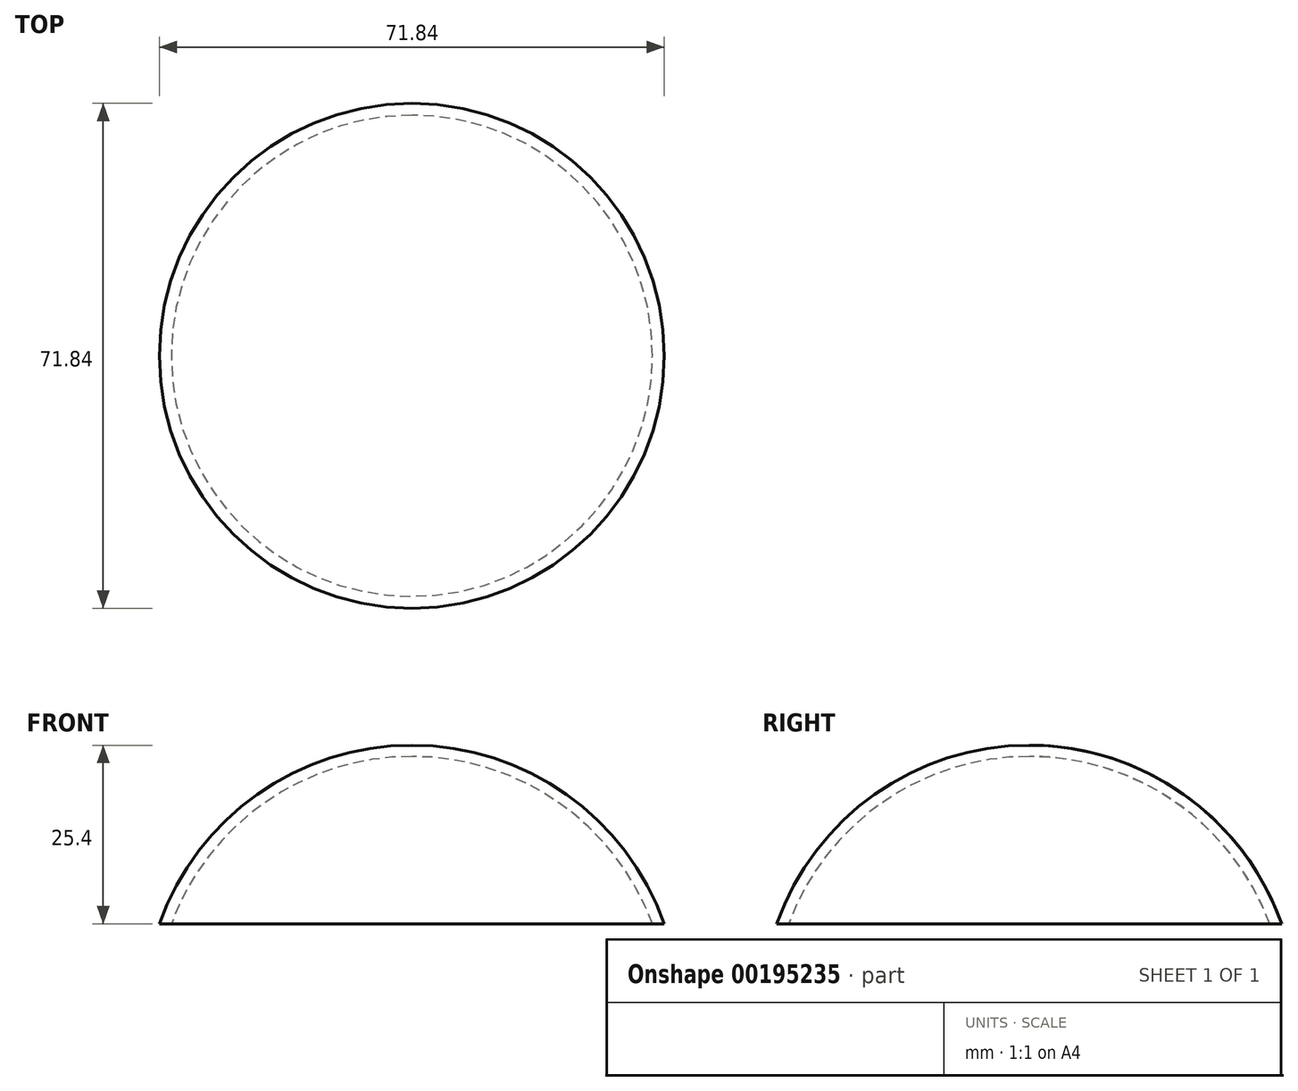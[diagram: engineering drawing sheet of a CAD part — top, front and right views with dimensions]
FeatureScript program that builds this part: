
annotation { "Feature Type Name" : "Feature", "Feature Type Description" : "" }
export const myFeature = defineFeature(function(context is Context, id is Id, definition is map)
    precondition{}
    {
        {
            var Q0;
            Q0=qCreatedBy(makeId("Right.planeOp"),FACE);
            var sketch = newSketch(context, id + "F0", { "sketchPlane" : qUnion([Q0])});
            skArc(sketch, "E0", {"start": v(38.1, 0) * mm, "mid": v(26.94, 26.94) * mm, "end": v(0, 38.1) * mm, "construction": true});
            skLineSegment(sketch, "E1", {"start": v(0, 38.1) * mm, "end": v(0, 0) * mm, "construction": true});
            skLineSegment(sketch, "E2", {"start": v(0, 0) * mm, "end": v(38.1, 0) * mm, "construction": true});
            skArc(sketch, "E3", {"start": v(36.51, 0) * mm, "mid": v(25.82, 25.82) * mm, "end": v(0, 36.51) * mm, "construction": true});
            skLineSegment(sketch, "E4", {"start": v(38.1, 0) * mm, "end": v(36.51, 0) * mm});
            skLineSegment(sketch, "E5", {"start": v(0, 36.51) * mm, "end": v(0, 38.1) * mm});
            skArc(sketch, "E6", {"start": v(34.23, 12.7) * mm, "mid": v(20.85, 29.97) * mm, "end": v(0, 36.51) * mm});
            skArc(sketch, "E7", {"start": v(35.92, 12.7) * mm, "mid": v(22, 31.1) * mm, "end": v(0, 38.1) * mm});
            skLineSegment(sketch, "E8", {"start": v(35.92, 12.7) * mm, "end": v(34.23, 12.7) * mm});
            skSolve(sketch);
        }
        {
            var Q0;
            Q0 = qSketchRegion(id + "F0", true);
            var Q1;
            Q1=sQuery(id+"F0.wireOp",EDGE,"E1");
            revolve(context, id + "F1", {"entities" : qUnion([Q0]), "axis" : qUnion([Q1]), "revolveType" : RevolveType.SYMMETRIC, "angle" : 360 * degree});
        }
    });
